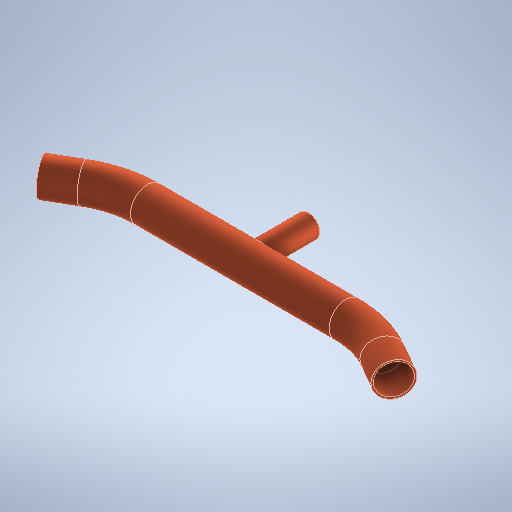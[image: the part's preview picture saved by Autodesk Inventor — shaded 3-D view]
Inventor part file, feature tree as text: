
AUTODESK INVENTOR PART (.ipt)
format: ipt  version: 2025.1 (Build 291241000, 241)  size: 320,000 bytes
history: native  units: mm
features: sketch x5, plane x3, sweep x2, other x1, extrude x1, mirror x1
ambient origin geometry x8: Origin, YZ Plane, XZ Plane, XY Plane, X Axis, Y Axis, Z Axis, Center Point
bodies: Solid1 (feature_tree), Solid3 (feature_tree)
feature tree (13):
  sketch  "Sketch3"  dims[d5=30.0deg d6=0.0mm d7=0.0mm]
  other  "Work Axis1"
  plane  "Work Plane3"
  sweep  "Sweep3"
  plane  "Work Plane4"
  extrude  "Extrusion1"  Depth=27.0mm
  sweep  "Sweep1"
  plane  "Work Plane1"
  mirror  "Mirror1"
  sketch  "Sketch1"  dims[d0=9.0mm d1=26.5mm]
  sketch  "Sketch2"  dims[d3=8.0mm d4=27.0mm]
  sketch  "Sketch4"  dims[d8=0.0mm]
  sketch  "Sketch5"  dims[d9=53.0mm d10=27.0mm d11=8.0mm d12=8.0mm d13=30.0deg d15=9.0mm d18=8.0mm d19=90.0deg d20=0.0mm d21=0.0mm d22=16.5mm d23=6.0mm d24=10.0mm d25=0.0mm d26=5.0mm]
